# Revit family: MINIVAC - PS
name_source: partatom
category: Equipement de génie climatique
revit_build: Autodesk Revit 2018 (Build: 20170223_1515(x64)
units: mm (PartAtom-declared; Revit-internal decimal feet)

## family parameters
Basée sur le plan de construction = Non
Classification = Aucun
Cote de connecteur circulaire = Utiliser le diamètre
Couper avec des vides une fois chargée = Non
Partagée = Non
Point de calcul de pièce = Non
Toujours verticalement = Oui
Type d'élément = Normal

## types (4) — shared parameters
BRANCHEMENT_TERRE = Oui
COFFRET ELEC = COFFRET ELEC STANDARD PM2 : COFFRET PM2 600x300x300
COS_PHI = 0.9
DESCR_ALIM_X = Alimentation électrique, 3G1.5mm²
DESCR_ALIM_Y = Alimentation électrique, 3G1.5mm²
DESCR_RESERV = 70L
DIAMETRE = 1200 mm  [stored 3.93701 ft]
DIAM_ASPI_VIDE = 15 mm  [stored 0.0492126 ft]
DIAM_PURGE = 15 mm  [stored 0.0492126 ft]
EP_BOUCH = 6.3 mm
EP_PATTE = 5 mm  [stored 0.0164042 ft]
Fabricant = MIL'S
HAUTEUR = 2100 mm
HAUT_FOND = 125 mm  [stored 0.410105 ft]
HAUT_LEVAGE = 52.4 mm
HAUT_VIROLE_PIED = 114.5 mm
LARG_PATTE 1 = 80 mm  [stored 0.262467 ft]
LARG_PATTE 2 = 80 mm  [stored 0.262467 ft]
LARG_PATTE 3 = 80 mm  [stored 0.262467 ft]
LONG_BOSS = 25 mm  [stored 0.082021 ft]
LONG_BOSS_BAS = 20 mm  [stored 0.0656168 ft]
LONG_BOSS_HAUT = 20 mm  [stored 0.0656168 ft]
LONG_BOUCH = 19 mm  [stored 0.062336 ft]
LONG_OUVERTURE = 125 mm  [stored 0.410105 ft]
LONG_VIROLE = 50 mm  [stored 0.164042 ft]
NBR_POLES = 1
NEUTRE = Oui
NIVEAU_SONORE(dB(A)) = 57
OFFSET_BOSS = 438 mm  [stored 1.43701 ft]
OFFSET_BOSS_BAS = 127 mm
OFFSET_HAUT_BOSS_1 = 850 mm  [stored 2.78871 ft]
OFFSET_HAUT_BOSS_2 = 1300 mm  [stored 4.26509 ft]
OFFSET_HAUT_BOSS_3 = 1600 mm  [stored 5.24934 ft]
OFFSET_HAUT_FOND = 70 mm  [stored 0.229659 ft]
OFFSET_PATTE_EXT 1 = 210 mm  [stored 0.688976 ft]
OFFSET_PATTE_EXT 2 = 210 mm  [stored 0.688976 ft]
OFFSET_PATTE_EXT 3 = 210 mm  [stored 0.688976 ft]
OFFSET_PATTE_INT 1 = 310 mm  [stored 1.01706 ft]
OFFSET_PATTE_INT 2 = 310 mm  [stored 1.01706 ft]
OFFSET_PATTE_INT 3 = 310 mm  [stored 1.01706 ft]
RAYON_PATTE = 375 mm  [stored 1.23031 ft]
RAY_BOUCH = 33 mm  [stored 0.108268 ft]
RAY_PAN_BOUCH = 19.8 mm  [stored 0.0649606 ft]
TENSION_ALIM = 230 V
ØBOSS = 66 mm  [stored 0.216535 ft]
ØBOSS_2 = 17.5 mm  [stored 0.0574147 ft]
ØBOSS_BAS = 26.5 mm  [stored 0.0869423 ft]
ØBOSS_HAUT = 26.5 mm  [stored 0.0869423 ft]
ØPATTE = 750 mm  [stored 2.46063 ft]
ØVIROLE = 650 mm  [stored 2.13255 ft]
ØVIROLE_BAS = 500 mm  [stored 1.64042 ft]
ØVIROLE_BAS_INT = 497 mm

## per-type parameters (varying)
| type | 3EME POMPE | DEBIT_ASPI_VIDE | DEBIT_REFOUL_VIDE | DESCR_ASPI | DESCR_REFOUL | POIDS(Kg) | POMPE | PUISS_APPARENTE_X | PUISS_APPARENTE_Y | PUISS_ELECT_X | PUISS_ELECT_Y |
| MINIVAC 3 - PS12V | Oui | 30.0 m³/h | 30.0 m³/h | Aspiration Vide; 3x10m3/h; G1/2"FEM | Refoulement Vide; 3x10m3/h; G1/2"FEM | 100 mm  [stored 0.328084 ft] | PAV PS : 12V | 644 VA | 1289 VA | 1 kW | 1 kW |
| MINIVAC 3 - PS7V | Oui | 19.2 m³/h | 19.2 m³/h | Aspiration Vide; 3x6.4m3/h; G1/2"FEM | Refoulement Vide; 3x6.4m3/h; G1/2"FEM | 100 mm  [stored 0.328084 ft] | PAV PS : 7V | 422 VA | 844 VA | 0 kW | 1 kW |
| MINIVAC 2 - PS12V | Non | 20.0 m³/h | 20.0 m³/h | Aspiration Vide; 2x10m3/h; G1/2"FEM | Refoulement Vide; 2x10m3/h; G1/2"FEM | 95 mm  [stored 0.31168 ft] | PAV PS : 12V | 644 VA | 644 VA | 1 kW | 1 kW |
| MINIVAC 2 - PS7V | Non | 12.8 m³/h | 12.8 m³/h | Aspiration Vide; 2x6.4m3/h; G1/2"FEM | Refoulement Vide; 2x6.4m3/h; G1/2"FEM | 95 mm  [stored 0.31168 ft] | PAV PS : 7V | 422 VA | 422 VA | 0 kW | 0 kW |

note: [stored X ft] marks values corroborated as IEEE doubles in the binary element streams (Revit-internal decimal feet)

## geometry (parser evidence)
native form markers: Sweep x5
no freeform markers — native parametric forms only
